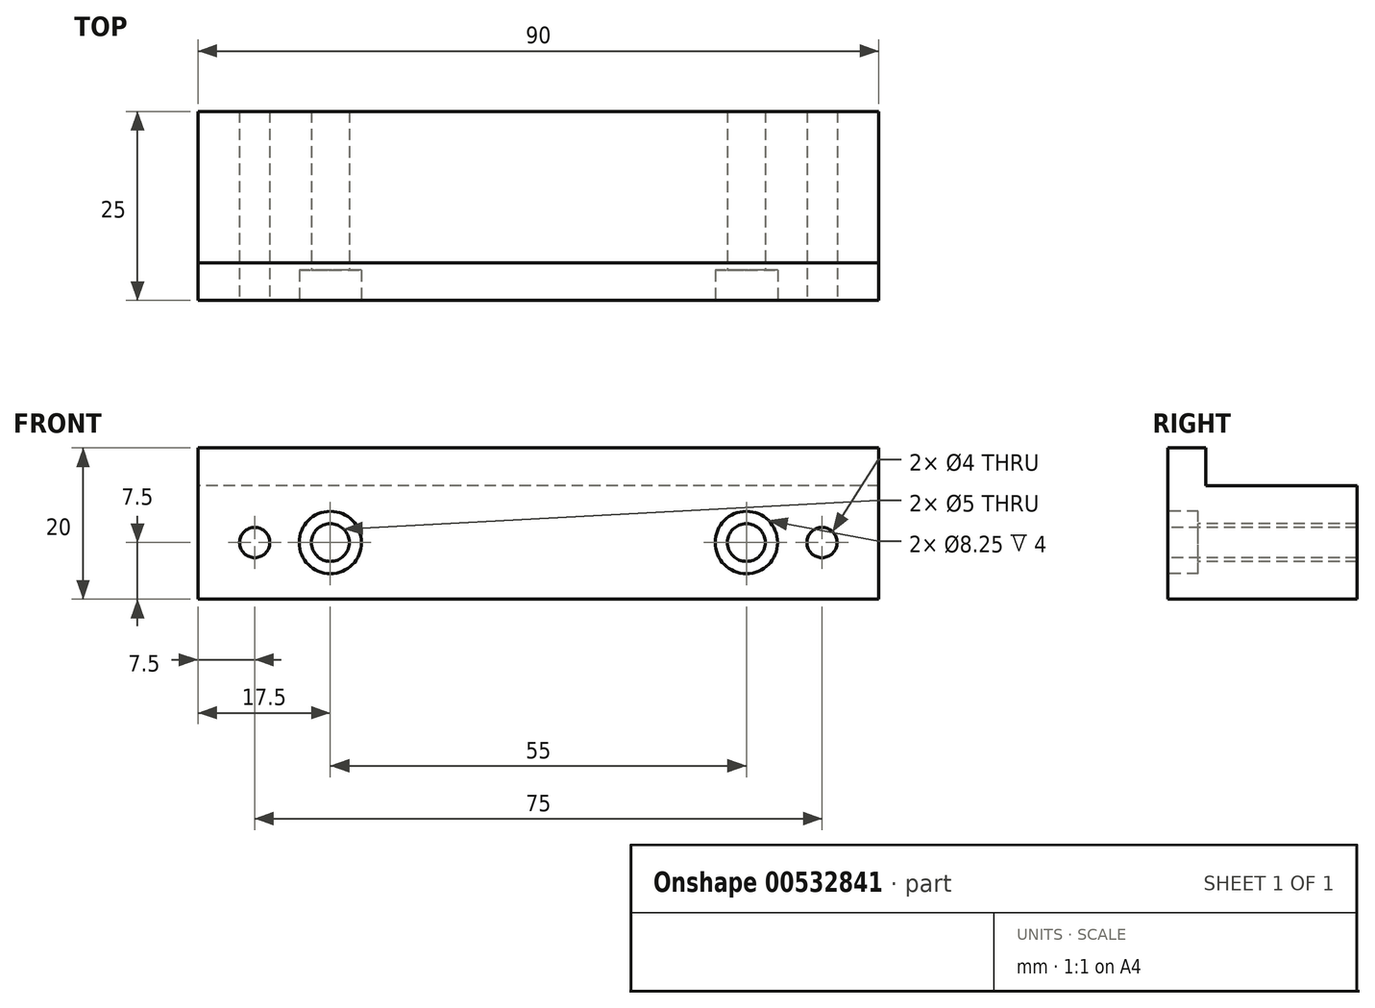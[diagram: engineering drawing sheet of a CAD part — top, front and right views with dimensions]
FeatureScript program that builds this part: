
annotation { "Feature Type Name" : "Feature", "Feature Type Description" : "" }
export const myFeature = defineFeature(function(context is Context, id is Id, definition is map)
    precondition{}
    {
        {
            var Q0;
            Q0=qCreatedBy(makeId("Right.planeOp"),FACE);
            var sketch = newSketch(context, id + "F0", { "sketchPlane" : qUnion([Q0])});
            skLineSegment(sketch, "E0", {"start": v(0, 0) * mm, "end": v(-25, 0) * mm});
            skLineSegment(sketch, "E1", {"start": v(-25, 0) * mm, "end": v(-25, 20) * mm});
            skLineSegment(sketch, "E2", {"start": v(-25, 20) * mm, "end": v(-20, 20) * mm});
            skLineSegment(sketch, "E3", {"start": v(-20, 20) * mm, "end": v(-20, 15) * mm});
            skLineSegment(sketch, "E4", {"start": v(-20, 15) * mm, "end": v(0, 15) * mm});
            skLineSegment(sketch, "E5", {"start": v(0, 15) * mm, "end": v(0, 0) * mm});
            skSolve(sketch);
        }
        {
            var Q0;
            Q0=qSketchRegion(id+"F0",true);
            extrude(context, id + "F1", {"entities" : qUnion([Q0]), "endBound" : BoundingType.SYMMETRIC, "depth" : 90 * mm, "offsetDistance" : 25 * mm});
        }
        {
            var Q0;
            Q0=makeQuery(id+"F1.opExtrude","SWEPT_FACE",FACE,{"disambiguationData":[OSD([sQuery(id+"F0.wireOp",EDGE,"E1")])]});
            var sketch = newSketch(context, id + "F2", { "sketchPlane" : qUnion([Q0])});
            skPoint(sketch, "E6", {"position": v(-27.5, 7.5) * mm});
            skPoint(sketch, "E7", {"position": v(27.5, 7.5) * mm});
            skCircle(sketch, "E8", {"center": v(-37.5, 7.5) * mm, "radius": 2 * mm});
            skCircle(sketch, "E9", {"center": v(37.5, 7.5) * mm, "radius": 2 * mm});
            skSolve(sketch);
        }
        {
            var Q0;
            Q0=makeQuery(id+"F2.imprint","IMPRINT",FACE,{"disambiguationData":[TD([[makeQuery(id+"F2.imprint","IMPRINT",EDGE,{"derivedFrom":sQuery(id+"F2.wireOp",EDGE,"E8")}),1.0]])]});
            var Q1;
            Q1=makeQuery(id+"F2.imprint","IMPRINT",FACE,{"disambiguationData":[TD([[makeQuery(id+"F2.imprint","IMPRINT",EDGE,{"derivedFrom":sQuery(id+"F2.wireOp",EDGE,"E9")}),1.0]])]});
            extrude(context, id + "F3", {"entities" : qUnion([Q0, Q1]), "operationType" : NewBodyOperationType.REMOVE, "endBound" : BoundingType.THROUGH_ALL, "oppositeDirection" : true, "depth" : 25 * mm, "offsetDistance" : 25 * mm});
        }
        {
            var Q0;
            Q0=sQuery(id+"F2.wireOp",VERTEX,"E6");
            var Q1;
            Q1=sQuery(id+"F2.wireOp",VERTEX,"E7");
            var Q2;
            Q2=makeQuery(id+"F1.opExtrude","SWEPT_BODY",BODY,{"disambiguationData":[OSD([sQuery(id+"F0.wireOp",EDGE,"E0"),sQuery(id+"F0.wireOp",EDGE,"E1"),sQuery(id+"F0.wireOp",EDGE,"E2"),sQuery(id+"F0.wireOp",EDGE,"E3"),sQuery(id+"F0.wireOp",EDGE,"E4"),sQuery(id+"F0.wireOp",EDGE,"E5")])]});
            hole(context, id + "F4", {"style" : HoleStyle.C_BORE, "endStyle" : HoleEndStyle.THROUGH, "standardTappedOrClearance" : lookupTablePath({ "standard" : "ISO", "size" : "5", "type" : "Drilled" }), "standardBlindInLast" : lookupTablePath({ "standard" : "ISO", "size" : "5", "type" : "Drilled" }), "holeDiameter" : 5 * mm, "cBoreDiameter" : 8.25 * mm, "cBoreDepth" : 4 * mm, "isTappedThrough" : true, "tappedDepth" : 10.9 * mm, "tapClearance" : 3, "locations" : qUnion([Q0, Q1]), "scope" : qUnion([Q2])});
        }
    });
